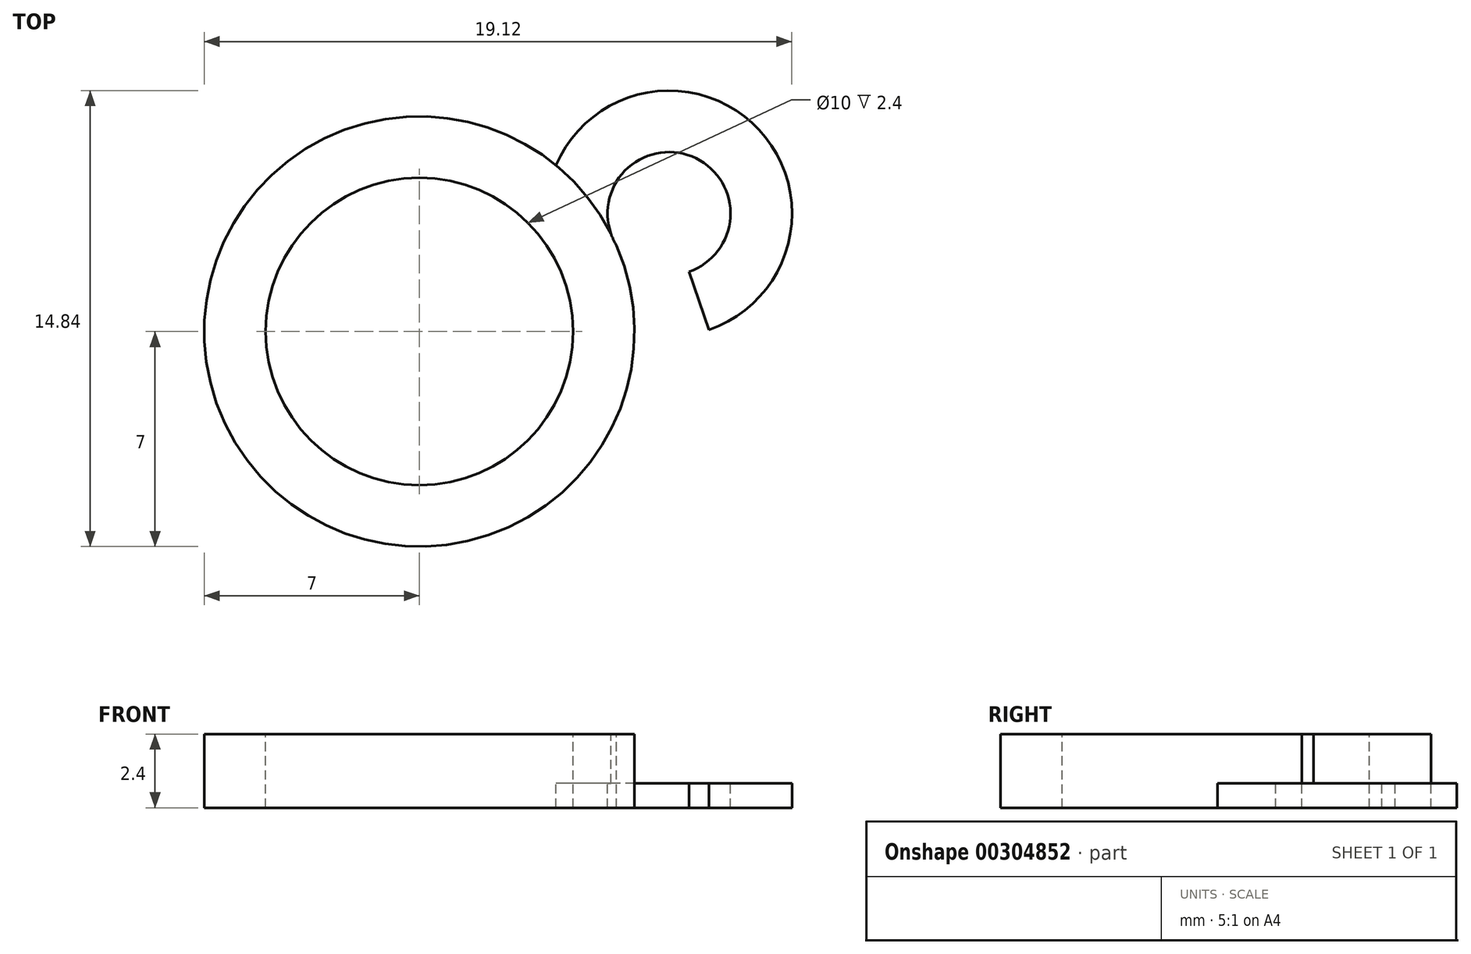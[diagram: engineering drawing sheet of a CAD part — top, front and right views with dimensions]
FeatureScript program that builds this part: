
annotation { "Feature Type Name" : "Feature", "Feature Type Description" : "" }
export const myFeature = defineFeature(function(context is Context, id is Id, definition is map)
    precondition{}
    {
        {
            var Q0;
            Q0=qCreatedBy(makeId("Top.planeOp"),FACE);
            var sketch = newSketch(context, id + "F0", { "sketchPlane" : qUnion([Q0])});
            skCircle(sketch, "E0", {"center": v(0, 0) * mm, "radius": 7 * mm});
            skCircle(sketch, "E1", {"center": v(0, 0) * mm, "radius": 5 * mm});
            skCircle(sketch, "E2", {"center": v(8.12, 3.84) * mm, "radius": 4 * mm});
            skPoint(sketch, "E2.first.point", {"position": v(7, 0) * mm});
            skPoint(sketch, "E2.second.point", {"position": v(11.72, 5.58) * mm});
            skPoint(sketch, "E2.third.point", {"position": v(4.62, 1.9) * mm});
            skCircle(sketch, "E3.0", {"center": v(8.12, 3.84) * mm, "radius": 2 * mm});
            skLineSegment(sketch, "E4", {"start": v(8.12, 3.84) * mm, "end": v(9.42, 0.05) * mm});
            skLineSegment(sketch, "E5", {"start": v(8.12, 3.84) * mm, "end": v(4.62, 1.9) * mm});
            skSolve(sketch);
        }
        {
            var Q0;
            {var subQ0=sQuery(id+"F0.wireOp",EDGE,"E2");var subQ1=sQuery(id+"F0.wireOp",EDGE,"E0");var subQ2=makeQuery(id+"F0.imprint","INTERSECT",VERTEX,{"disambiguationData":[OD(1.0)],"derivedFrom":[subQ1,subQ0]});Q0=makeQuery(id+"F0.imprint","IMPRINT",FACE,{"disambiguationData":[TD([[makeQuery(id+"F0.imprint","IMPRINT",EDGE,{"disambiguationData":[TD([[subQ2,1.0]])],"derivedFrom":subQ1}),1.0]])]});}
            var Q1;
            {var subQ1=sQuery(id+"F0.wireOp",EDGE,"E2");var subQ5=sQuery(id+"F0.wireOp",EDGE,"E0");var subQ6=makeQuery(id+"F0.imprint","INTERSECT",VERTEX,{"disambiguationData":[OD(1.0)],"derivedFrom":[subQ5,subQ1]});Q1=makeQuery(id+"F0.imprint","IMPRINT",FACE,{"disambiguationData":[TD([[makeQuery(id+"F0.imprint","IMPRINT",EDGE,{"disambiguationData":[TD([[subQ6,1.0]])],"derivedFrom":subQ5}),-1.0]])]});}
            var Q2;
            {var subQ0=sQuery(id+"F0.wireOp",EDGE,"E2");var subQ1=sQuery(id+"F0.wireOp",EDGE,"E0");var subQ2=makeQuery(id+"F0.imprint","INTERSECT",VERTEX,{"disambiguationData":[OD(0.0)],"derivedFrom":[subQ1,subQ0]});Q2=makeQuery(id+"F0.imprint","IMPRINT",FACE,{"disambiguationData":[TD([[makeQuery(id+"F0.imprint","IMPRINT",EDGE,{"disambiguationData":[TD([[subQ2,1.0]])],"derivedFrom":subQ1}),1.0]])]});}
            var Q3;
            {var subQ0=sQuery(id+"F0.wireOp",EDGE,"E2");var subQ1=sQuery(id+"F0.wireOp",EDGE,"E0");var subQ2=makeQuery(id+"F0.imprint","INTERSECT",VERTEX,{"disambiguationData":[OD(0.0)],"derivedFrom":[subQ1,subQ0]});Q3=makeQuery(id+"F0.imprint","IMPRINT",FACE,{"disambiguationData":[TD([[makeQuery(id+"F0.imprint","IMPRINT",EDGE,{"disambiguationData":[TD([[subQ2,-1.0]])],"derivedFrom":subQ1}),1.0]])]});}
            extrude(context, id + "F1", {"entities" : qUnion([Q0, Q1, Q2, Q3]), "oppositeDirection" : true, "depth" : 2.4 * mm});
        }
        {
            var Q0;
            {var subQ0=sQuery(id+"F0.wireOp",EDGE,"E2");var subQ1=sQuery(id+"F0.wireOp",EDGE,"E0");var subQ2=makeQuery(id+"F0.imprint","INTERSECT",VERTEX,{"disambiguationData":[OD(1.0)],"derivedFrom":[subQ1,subQ0]});Q0=makeQuery(id+"F0.imprint","IMPRINT",FACE,{"disambiguationData":[TD([[makeQuery(id+"F0.imprint","IMPRINT",EDGE,{"disambiguationData":[TD([[subQ2,1.0]])],"derivedFrom":subQ1}),-1.0]])]});}
            extrude(context, id + "F2", {"entities" : qUnion([Q0]), "operationType" : NewBodyOperationType.REMOVE, "oppositeDirection" : true, "depth" : 1.6 * mm});
        }
    });
